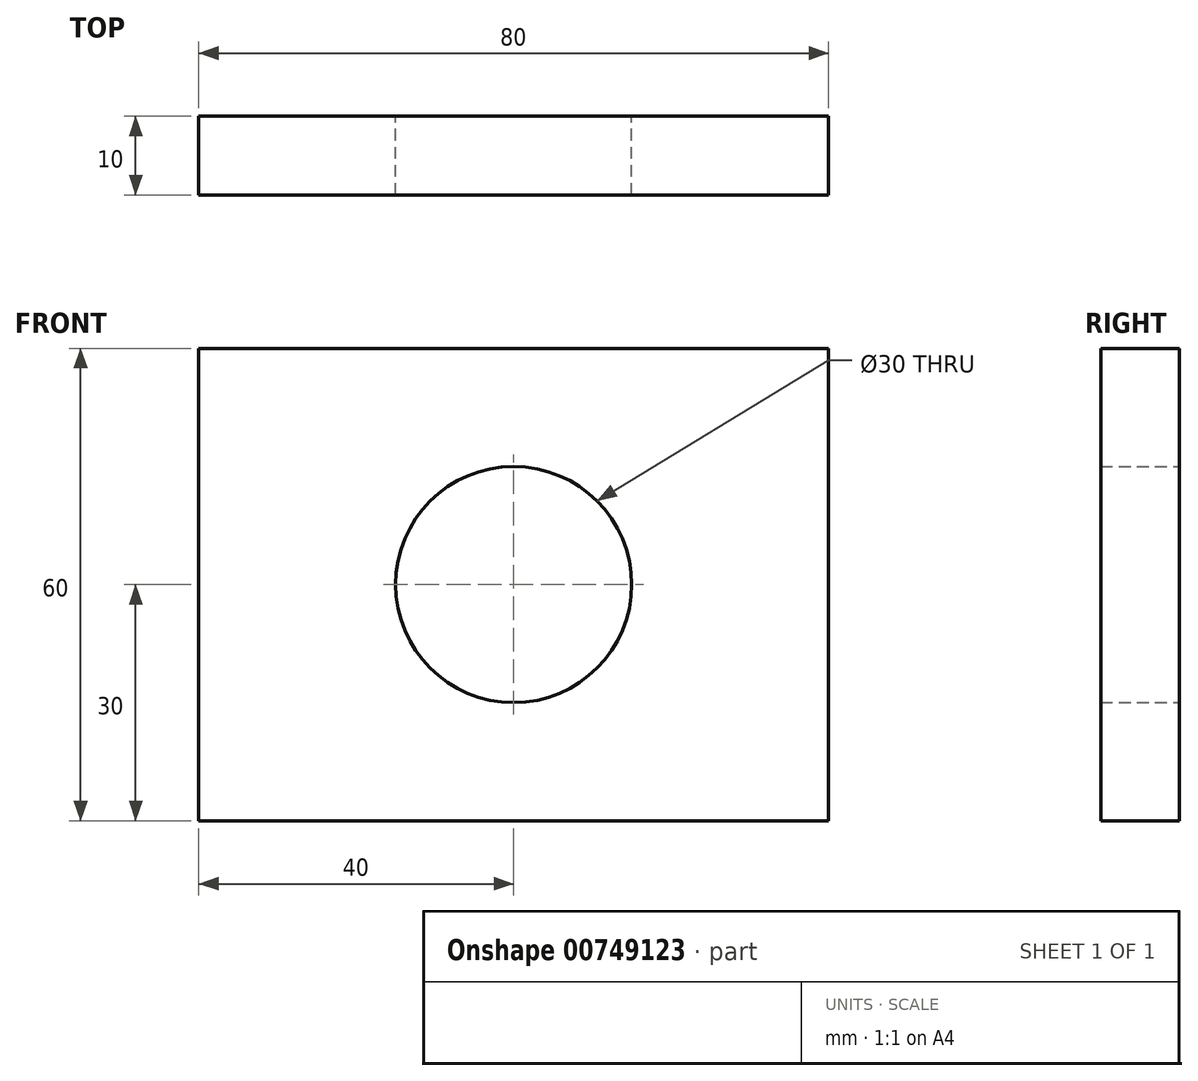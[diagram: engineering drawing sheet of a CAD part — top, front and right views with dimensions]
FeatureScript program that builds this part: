
annotation { "Feature Type Name" : "Feature", "Feature Type Description" : "" }
export const myFeature = defineFeature(function(context is Context, id is Id, definition is map)
    precondition{}
    {
        {
            var Q0;
            Q0=qCreatedBy(makeId("Front.planeOp"),FACE);
            var sketch = newSketch(context, id + "F0", { "sketchPlane" : qUnion([Q0])});
            skLineSegment(sketch, "E0.bottom", {"start": v(-40, 30) * mm, "end": v(40, 30) * mm});
            skLineSegment(sketch, "E0.top", {"start": v(-40, -30) * mm, "end": v(40, -30) * mm});
            skLineSegment(sketch, "E0.left", {"start": v(-40, 30) * mm, "end": v(-40, -30) * mm});
            skLineSegment(sketch, "E0.right", {"start": v(40, 30) * mm, "end": v(40, -30) * mm});
            skPoint(sketch, "E0.middle", {"position": v(0, 0) * mm});
            skCircle(sketch, "E1", {"center": v(0, 0) * mm, "radius": 15 * mm});
            skSolve(sketch);
        }
        {
            var Q0;
            Q0=makeQuery(id+"F0.imprint","IMPRINT",FACE,{"disambiguationData":[TD([[makeQuery(id+"F0.imprint","IMPRINT",EDGE,{"derivedFrom":sQuery(id+"F0.wireOp",EDGE,"E0.bottom")}),-1.0]])]});
            extrude(context, id + "F1", {"entities" : qUnion([Q0]), "depth" : 10 * mm, "offsetDistance" : 25 * mm});
        }
    });
